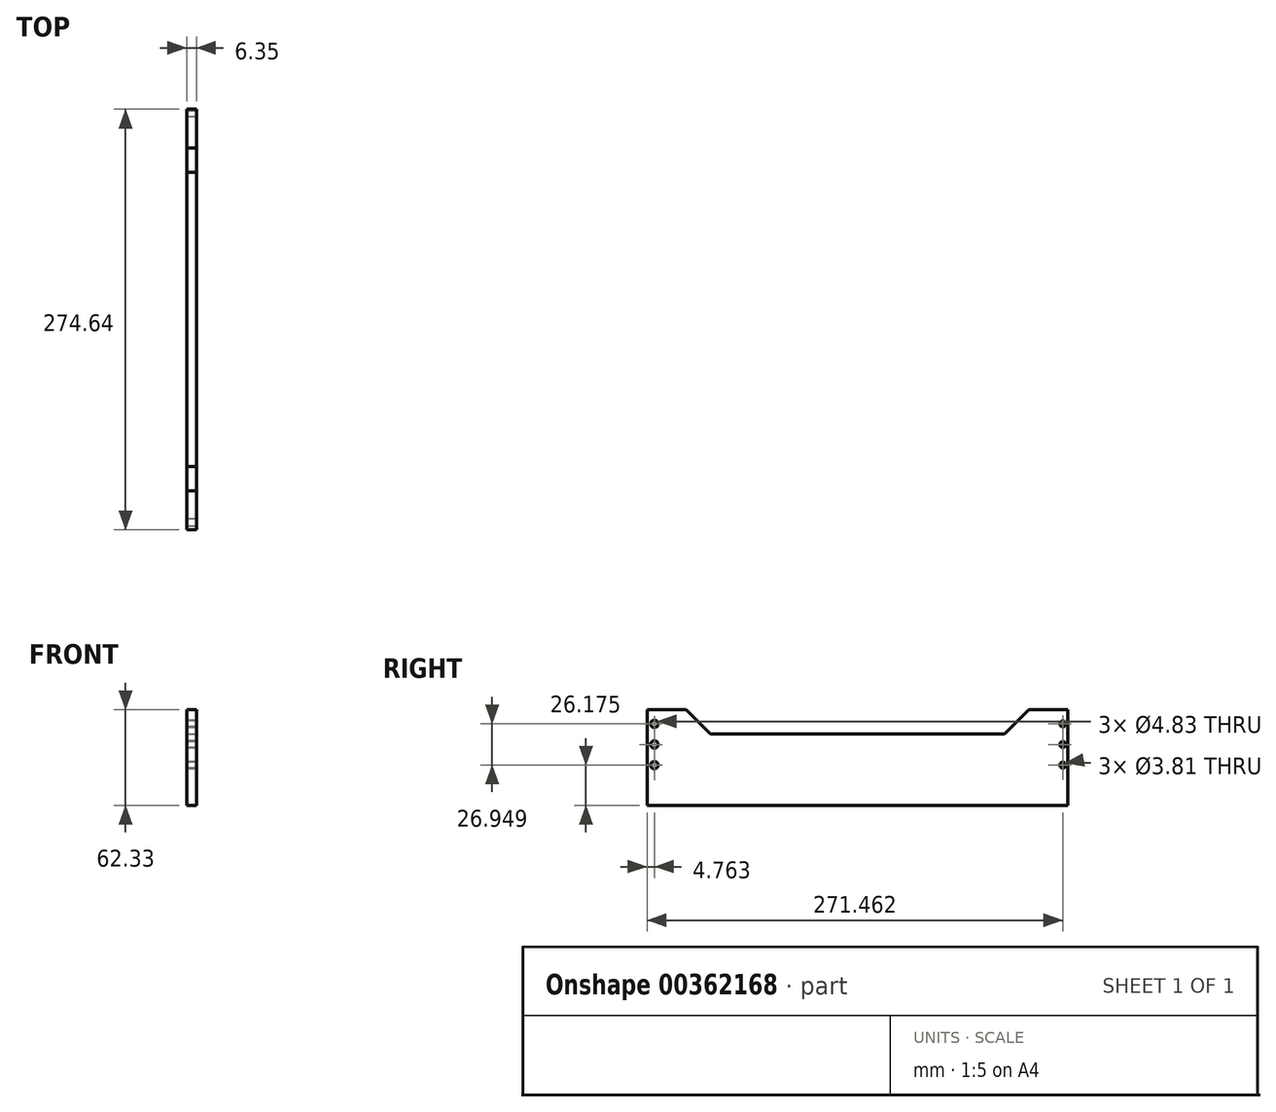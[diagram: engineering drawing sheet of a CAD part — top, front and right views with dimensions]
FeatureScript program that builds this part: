
annotation { "Feature Type Name" : "Feature", "Feature Type Description" : "" }
export const myFeature = defineFeature(function(context is Context, id is Id, definition is map)
    precondition{}
    {
        {
            var Q0;
            Q0=qCreatedBy(makeId("Right.planeOp"),FACE);
            var sketch = newSketch(context, id + "F0", { "sketchPlane" : qUnion([Q0])});
            skLineSegment(sketch, "E0", {"start": v(274.64, 0) * mm, "end": v(274.64, 53.9) * mm});
            skLineSegment(sketch, "E1", {"start": v(274.64, 53.9) * mm, "end": v(0, 53.9) * mm});
            skLineSegment(sketch, "E2", {"start": v(0, 53.9) * mm, "end": v(0, 0) * mm});
            skLineSegment(sketch, "E3", {"start": v(9.52, 53.9) * mm, "end": v(9.52, 0) * mm, "construction": true});
            skLineSegment(sketch, "E4", {"start": v(9.52, 26.95) * mm, "end": v(0, 26.95) * mm, "construction": true});
            skLineSegment(sketch, "E5", {"start": v(4.76, 0) * mm, "end": v(4.76, 26.95) * mm, "construction": true});
            skPoint(sketch, "E5.startSnap0", {"position": v(4.76, 26.95) * mm});
            skLineSegment(sketch, "E6", {"start": v(4.76, 26.95) * mm, "end": v(4.76, 53.9) * mm, "construction": true});
            skPoint(sketch, "E7", {"position": v(4.76, 40.42) * mm});
            skPoint(sketch, "E8", {"position": v(4.76, 13.47) * mm});
            skLineSegment(sketch, "E9", {"start": v(203.2, 53.9) * mm, "end": v(203.2, 0) * mm, "construction": true});
            skLineSegment(sketch, "E10", {"start": v(0, 0) * mm, "end": v(0, -12.7) * mm});
            skLineSegment(sketch, "E11", {"start": v(0, -12.7) * mm, "end": v(274.64, -12.7) * mm});
            skLineSegment(sketch, "E12", {"start": v(274.64, -12.7) * mm, "end": v(274.64, 0) * mm});
            skLineSegment(sketch, "E13", {"start": v(0, 0) * mm, "end": v(274.64, 0) * mm, "construction": true});
            skLineSegment(sketch, "E14", {"start": v(268.29, 53.9) * mm, "end": v(268.29, 0) * mm, "construction": true});
            skLineSegment(sketch, "E15", {"start": v(268.29, 26.95) * mm, "end": v(274.64, 26.95) * mm, "construction": true});
            skPoint(sketch, "E16.startSnap0", {"position": v(271.46, 26.95) * mm});
            skLineSegment(sketch, "E17", {"start": v(271.46, 0) * mm, "end": v(271.46, 26.95) * mm, "construction": true});
            skLineSegment(sketch, "E18", {"start": v(271.46, 53.9) * mm, "end": v(271.46, 26.95) * mm, "construction": true});
            skPoint(sketch, "E19", {"position": v(271.46, 40.42) * mm});
            skPoint(sketch, "E20", {"position": v(271.46, 13.47) * mm});
            skSolve(sketch);
        }
        {
            var Q0;
            Q0=makeQuery(id+"F0.imprint","IMPRINT",FACE,{"disambiguationData":[TD([[makeQuery(id+"F0.imprint","IMPRINT",EDGE,{"derivedFrom":sQuery(id+"F0.wireOp",EDGE,"E0")}),1.0]])]});
            extrude(context, id + "F1", {"entities" : qUnion([Q0]), "depth" : 6.35 * mm});
        }
        {
            var Q0;
            Q0=sQuery(id+"F0.wireOp",VERTEX,"E7");
            var Q1;
            Q1=sQuery(id+"F0.wireOp",VERTEX,"E5.startSnap0");
            var Q2;
            Q2=sQuery(id+"F0.wireOp",VERTEX,"E8");
            var Q3;
            Q3=sQuery(id+"F0.wireOp",VERTEX,"5ab4f9db-b021-4d52-971f-cab435579fd2");
            var Q4;
            Q4=makeQuery(id+"F1.opExtrude","SWEPT_BODY",BODY,{"disambiguationData":[OSD([sQuery(id+"F0.wireOp",EDGE,"LokPoCD6-FjNM-1Vt9-Nqnl-R2dUqbxLQ1ov"),sQuery(id+"F0.wireOp",EDGE,"E0"),sQuery(id+"F0.wireOp",EDGE,"E1"),sQuery(id+"F0.wireOp",EDGE,"E2")])]});
            hole(context, id + "F2", {"style" : HoleStyle.SIMPLE, "endStyle" : HoleEndStyle.THROUGH, "oppositeDirection" : true, "holeDiameter" : 4.83 * mm, "isTappedThrough" : true, "tappedDepth" : 12.7 * mm, "tapClearance" : 3, "startFromSketch" : true, "locations" : qUnion([Q0, Q1, Q2, Q3]), "scope" : qUnion([Q4])});
        }
        {
            var Q0;
            Q0=sQuery(id+"F0.wireOp",VERTEX,"E19");
            var Q1;
            Q1=sQuery(id+"F0.wireOp",VERTEX,"E16.startSnap0");
            var Q2;
            Q2=sQuery(id+"F0.wireOp",VERTEX,"E20");
            var Q3;
            Q3=makeQuery(id+"F1.opExtrude","SWEPT_BODY",BODY,{"disambiguationData":[OSD([sQuery(id+"F0.wireOp",EDGE,"E0"),sQuery(id+"F0.wireOp",EDGE,"E1"),sQuery(id+"F0.wireOp",EDGE,"E2"),sQuery(id+"F0.wireOp",EDGE,"E10"),sQuery(id+"F0.wireOp",EDGE,"E11"),sQuery(id+"F0.wireOp",EDGE,"E12")])]});
            hole(context, id + "F3", {"style" : HoleStyle.SIMPLE, "endStyle" : HoleEndStyle.THROUGH, "oppositeDirection" : true, "holeDiameter" : 3.8 * mm, "isTappedThrough" : true, "tappedDepth" : 12.7 * mm, "tapClearance" : 3, "startFromSketch" : true, "locations" : qUnion([Q0, Q1, Q2]), "scope" : qUnion([Q3])});
        }
        {
            var Q0;
            Q0=makeQuery(id+"F1.opExtrude","CAP_FACE",FACE,{"disambiguationData":[OSD([sQuery(id+"F0.wireOp",EDGE,"E0"),sQuery(id+"F0.wireOp",EDGE,"E1"),sQuery(id+"F0.wireOp",EDGE,"E2"),sQuery(id+"F0.wireOp",EDGE,"E10"),sQuery(id+"F0.wireOp",EDGE,"E11"),sQuery(id+"F0.wireOp",EDGE,"E12")])],"isStart":false});
            var sketch = newSketch(context, id + "F4", { "sketchPlane" : qUnion([Q0])});
            skLineSegment(sketch, "E21", {"start": v(0, 49.63) * mm, "end": v(25.4, 49.63) * mm});
            skLineSegment(sketch, "E22", {"start": v(249.24, 49.63) * mm, "end": v(233.36, 33.76) * mm});
            skLineSegment(sketch, "E23", {"start": v(233.36, 33.76) * mm, "end": v(41.28, 33.76) * mm});
            skLineSegment(sketch, "E24", {"start": v(41.28, 33.76) * mm, "end": v(25.4, 49.63) * mm});
            skLineSegment(sketch, "E25.trimOffspring", {"start": v(249.24, 49.63) * mm, "end": v(274.64, 49.63) * mm});
            skSolve(sketch);
        }
        {
            var Q0;
            {var subQ8=sQuery(id+"F4.wireOp",EDGE,"E21");Q0=makeQuery(id+"F4.imprint","IMPRINT",FACE,{"disambiguationData":[TD([[makeQuery(id+"F4.imprint","IMPRINT",EDGE,{"derivedFrom":subQ8}),1.0]])]});}
            extrude(context, id + "F5", {"entities" : qUnion([Q0]), "operationType" : NewBodyOperationType.REMOVE, "oppositeDirection" : true, "depth" : 25.4 * mm, "offsetDistance" : 25.4 * mm});
        }
    });
